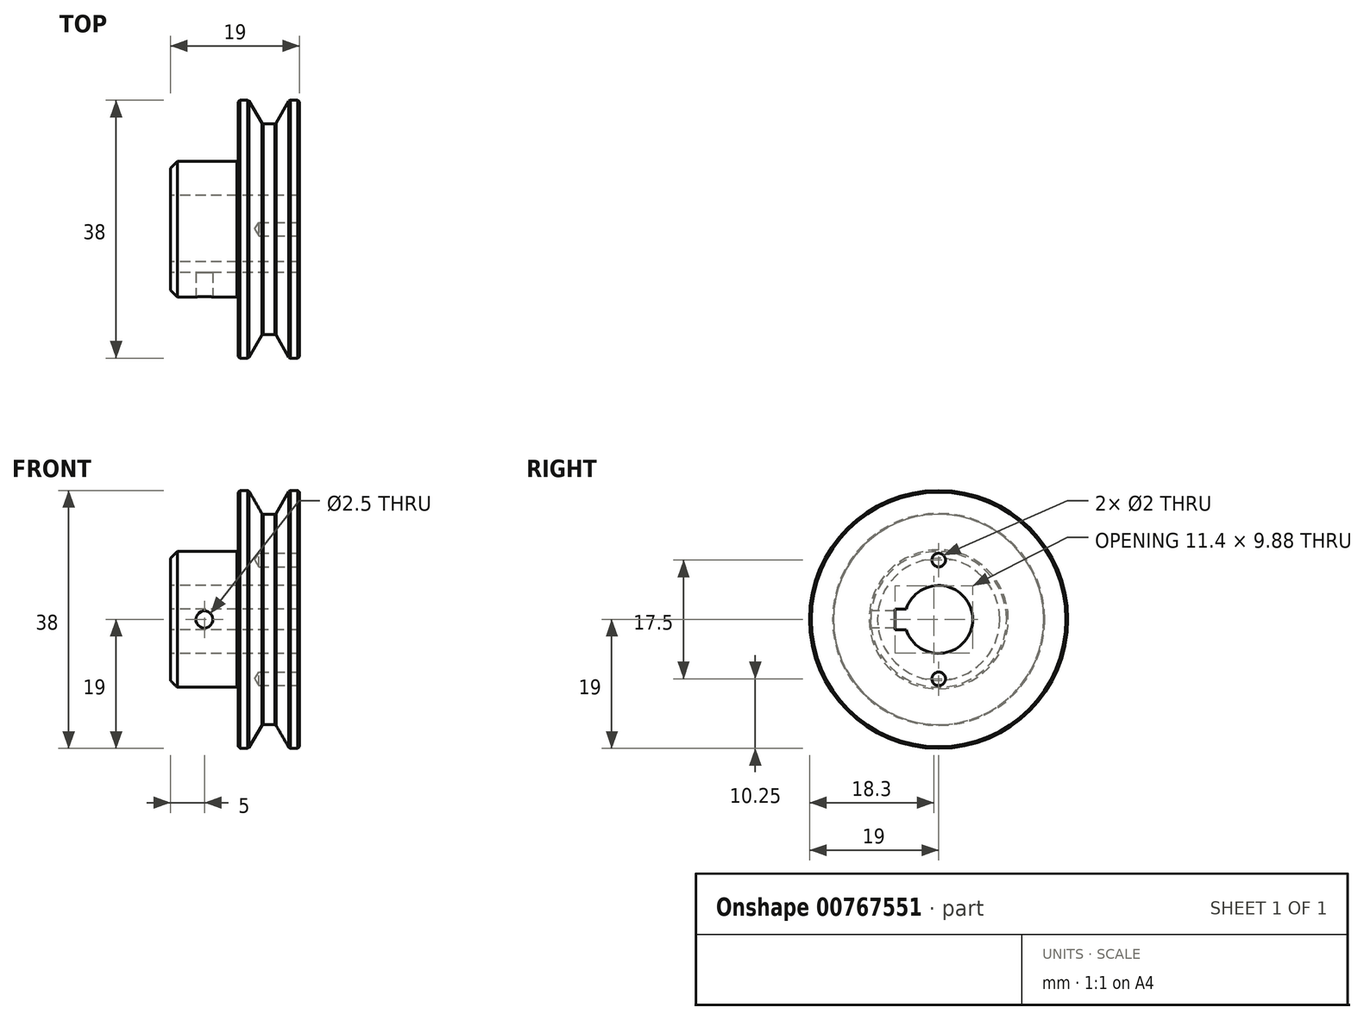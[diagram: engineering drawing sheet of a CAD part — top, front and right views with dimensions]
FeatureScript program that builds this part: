
annotation { "Feature Type Name" : "Feature", "Feature Type Description" : "" }
export const myFeature = defineFeature(function(context is Context, id is Id, definition is map)
    precondition{}
    {
        {
            var Q0;
            Q0=qCreatedBy(makeId("Front.planeOp"),FACE);
            var sketch = newSketch(context, id + "F0", { "sketchPlane" : qUnion([Q0])});
            skLineSegment(sketch, "E0", {"start": v(0, 0) * mm, "end": v(0, 10) * mm});
            skLineSegment(sketch, "E1", {"start": v(0, 10) * mm, "end": v(10, 10) * mm});
            skLineSegment(sketch, "E2", {"start": v(10, 10) * mm, "end": v(10, 19) * mm});
            skLineSegment(sketch, "E3", {"start": v(10, 19) * mm, "end": v(11.5, 19) * mm});
            skLineSegment(sketch, "E4", {"start": v(11.5, 19) * mm, "end": v(13.52, 15.5) * mm});
            skLineSegment(sketch, "E5", {"start": v(13.52, 15.5) * mm, "end": v(15.48, 15.5) * mm});
            skLineSegment(sketch, "E6", {"start": v(15.48, 15.5) * mm, "end": v(17.5, 19) * mm});
            skLineSegment(sketch, "E7", {"start": v(17.5, 19) * mm, "end": v(19, 19) * mm});
            skLineSegment(sketch, "E8", {"start": v(19, 19) * mm, "end": v(19, 0) * mm});
            skLineSegment(sketch, "E9", {"start": v(19, 0) * mm, "end": v(0, 0) * mm});
            skLineSegment(sketch, "E10", {"start": v(14.5, 15.5) * mm, "end": v(14.5, 19) * mm, "construction": true});
            skSolve(sketch);
        }
        {
            var Q0;
            Q0=qCreatedBy(makeId("Front.planeOp"),FACE);
            cPlane(context, id + "F1", {"entities" : qUnion([Q0]), "cplaneType" : CPlaneType.OFFSET, "offset" : 10 * mm, "width" : 150 * mm, "height" : 150 * mm});
        }
        {
            var Q0;
            Q0=makeQuery(id+"F0.imprint","IMPRINT",FACE,{"disambiguationData":[TD([[makeQuery(id+"F0.imprint","IMPRINT",EDGE,{"derivedFrom":sQuery(id+"F0.wireOp",EDGE,"E0")}),-1.0]])]});
            var Q1;
            Q1=sQuery(id+"F0.wireOp",EDGE,"E9");
            revolve(context, id + "F2", {"surfaceOperationType" : NewSurfaceOperationType.NEW, "entities" : qUnion([Q0]), "axis" : qUnion([Q1]), "revolveType" : RevolveType.FULL});
        }
        {
            var Q0;
            Q0=makeQuery(id+"F2.opRevolve","SWEPT_EDGE",EDGE,{"disambiguationData":[OSD([sQuery(id+"F0.wireOp",EDGE,"E0"),sQuery(id+"F0.wireOp",EDGE,"E1")])]});
            chamfer(context, id + "F3", {"entities" : qUnion([Q0]), "width" : 1 * mm, "tangentPropagation" : true});
        }
        {
            var Q0;
            Q0=makeQuery(id+"F2.opRevolve","SWEPT_FACE",FACE,{"disambiguationData":[OSD([sQuery(id+"F0.wireOp",EDGE,"E3")])]});
            var Q1;
            Q1=makeQuery(id+"F2.opRevolve","SWEPT_FACE",FACE,{"disambiguationData":[OSD([sQuery(id+"F0.wireOp",EDGE,"E7")])]});
            var Q2;
            Q2=makeQuery(id+"F2.opRevolve","SWEPT_EDGE",EDGE,{"disambiguationData":[OSD([sQuery(id+"F0.wireOp",EDGE,"E1"),sQuery(id+"F0.wireOp",EDGE,"E2")])]});
            var Q3;
            Q3=makeQuery(id+"F2.opRevolve","SWEPT_FACE",FACE,{"disambiguationData":[OSD([sQuery(id+"F0.wireOp",EDGE,"E5")])]});
            chamfer(context, id + "F4", {"entities" : qUnion([Q0, Q1, Q2, Q3]), "width" : 0.25 * mm, "tangentPropagation" : true});
        }
        {
            var Q0;
            Q0=qCreatedBy(makeId("Right.planeOp"),FACE);
            var sketch = newSketch(context, id + "F5", { "sketchPlane" : qUnion([Q0])});
            skArc(sketch, "E11", {"start": v(-4.77, -1.5) * mm, "mid": v(5, 0) * mm, "end": v(-4.77, 1.5) * mm});
            skLineSegment(sketch, "E12.bottom", {"start": v(-6.4, -1.5) * mm, "end": v(-4.77, -1.5) * mm});
            skLineSegment(sketch, "E12.top", {"start": v(-6.4, 1.5) * mm, "end": v(-4.77, 1.5) * mm});
            skLineSegment(sketch, "E12.left", {"start": v(-6.4, -1.5) * mm, "end": v(-6.4, 1.5) * mm});
            skPoint(sketch, "E12.middle", {"position": v(-2.92, 0) * mm});
            skPoint(sketch, "E13.orphan", {"position": v(0.57, 1.5) * mm});
            skPoint(sketch, "E14.orphan", {"position": v(0.57, -1.5) * mm});
            skSolve(sketch);
        }
        {
            var Q0;
            Q0 = qSketchRegion(id + "F5", true);
            var Q1;
            Q1=makeQuery(id+"F2.opRevolve","SWEPT_FACE",FACE,{"disambiguationData":[OSD([sQuery(id+"F0.wireOp",EDGE,"E8")])]});
            extrude(context, id + "F6", {"entities" : qUnion([Q0]), "operationType" : NewBodyOperationType.REMOVE, "endBound" : BoundingType.UP_TO_SURFACE, "depth" : 25 * mm, "endBoundEntityFace" : qUnion([Q1]), "offsetDistance" : 25 * mm});
        }
        {
            var Q0;
            Q0=qCreatedBy(id+"F1.planeOp",FACE);
            var sketch = newSketch(context, id + "F7", { "sketchPlane" : qUnion([Q0])});
            skPoint(sketch, "E15", {"position": v(5, 0) * mm});
            skSolve(sketch);
        }
        {
            var Q0;
            Q0=sQuery(id+"F7.wireOp",VERTEX,"E15");
            var Q1;
            Q1=makeQuery(id+"F2.opRevolve","SWEPT_BODY",BODY,{"disambiguationData":[OSD([sQuery(id+"F0.wireOp",EDGE,"E0"),sQuery(id+"F0.wireOp",EDGE,"E1"),sQuery(id+"F0.wireOp",EDGE,"E2"),sQuery(id+"F0.wireOp",EDGE,"E3"),sQuery(id+"F0.wireOp",EDGE,"E4"),sQuery(id+"F0.wireOp",EDGE,"E5"),sQuery(id+"F0.wireOp",EDGE,"E6"),sQuery(id+"F0.wireOp",EDGE,"E7"),sQuery(id+"F0.wireOp",EDGE,"E8"),sQuery(id+"F0.wireOp",EDGE,"E9")])]});
            hole(context, id + "F8", {"style" : HoleStyle.SIMPLE, "endStyle" : HoleEndStyle.BLIND, "standardTappedOrClearance" : lookupTablePath({ "standard" : "ISO", "engagement" : "75%", "pitch" : "0.5 mm", "size" : "M3", "type" : "Tapped" }), "standardBlindInLast" : lookupTablePath({ "standard" : "ISO", "engagement" : "75%", "pitch" : "0.5 mm", "size" : "M3", "type" : "Tapped" }), "holeDiameter" : 2.5 * mm, "majorDiameter" : 3 * mm, "showTappedDepth" : true, "holeDepth" : 14.2 * mm, "tappedDepth" : 12.2 * mm, "tapClearance" : 4, "startFromSketch" : true, "locations" : qUnion([Q0]), "scope" : qUnion([Q1])});
        }
        {
            var Q0;
            Q0=makeQuery(id+"F2.opRevolve","SWEPT_FACE",FACE,{"disambiguationData":[OSD([sQuery(id+"F0.wireOp",EDGE,"E8")])]});
            var sketch = newSketch(context, id + "F9", { "sketchPlane" : qUnion([Q0])});
            skPoint(sketch, "E16", {"position": v(0, 8.75) * mm});
            skPoint(sketch, "E17", {"position": v(0, -8.75) * mm});
            skSolve(sketch);
        }
        {
            var Q0;
            Q0=sQuery(id+"F9.wireOp",VERTEX,"E16");
            var Q1;
            Q1=sQuery(id+"F9.wireOp",VERTEX,"E17");
            var Q2;
            Q2=makeQuery(id+"F2.opRevolve","SWEPT_BODY",BODY,{"disambiguationData":[OSD([sQuery(id+"F0.wireOp",EDGE,"E0"),sQuery(id+"F0.wireOp",EDGE,"E1"),sQuery(id+"F0.wireOp",EDGE,"E2"),sQuery(id+"F0.wireOp",EDGE,"E3"),sQuery(id+"F0.wireOp",EDGE,"E4"),sQuery(id+"F0.wireOp",EDGE,"E5"),sQuery(id+"F0.wireOp",EDGE,"E6"),sQuery(id+"F0.wireOp",EDGE,"E7"),sQuery(id+"F0.wireOp",EDGE,"E8"),sQuery(id+"F0.wireOp",EDGE,"E9")])]});
            hole(context, id + "F10", {"style" : HoleStyle.SIMPLE, "endStyle" : HoleEndStyle.BLIND, "holeDiameter" : 2 * mm, "majorDiameter" : 3 * mm, "holeDepth" : 6 * mm, "tappedDepth" : 12.2 * mm, "tapClearance" : 4, "startFromSketch" : true, "locations" : qUnion([Q0, Q1]), "scope" : qUnion([Q2])});
        }
    });
